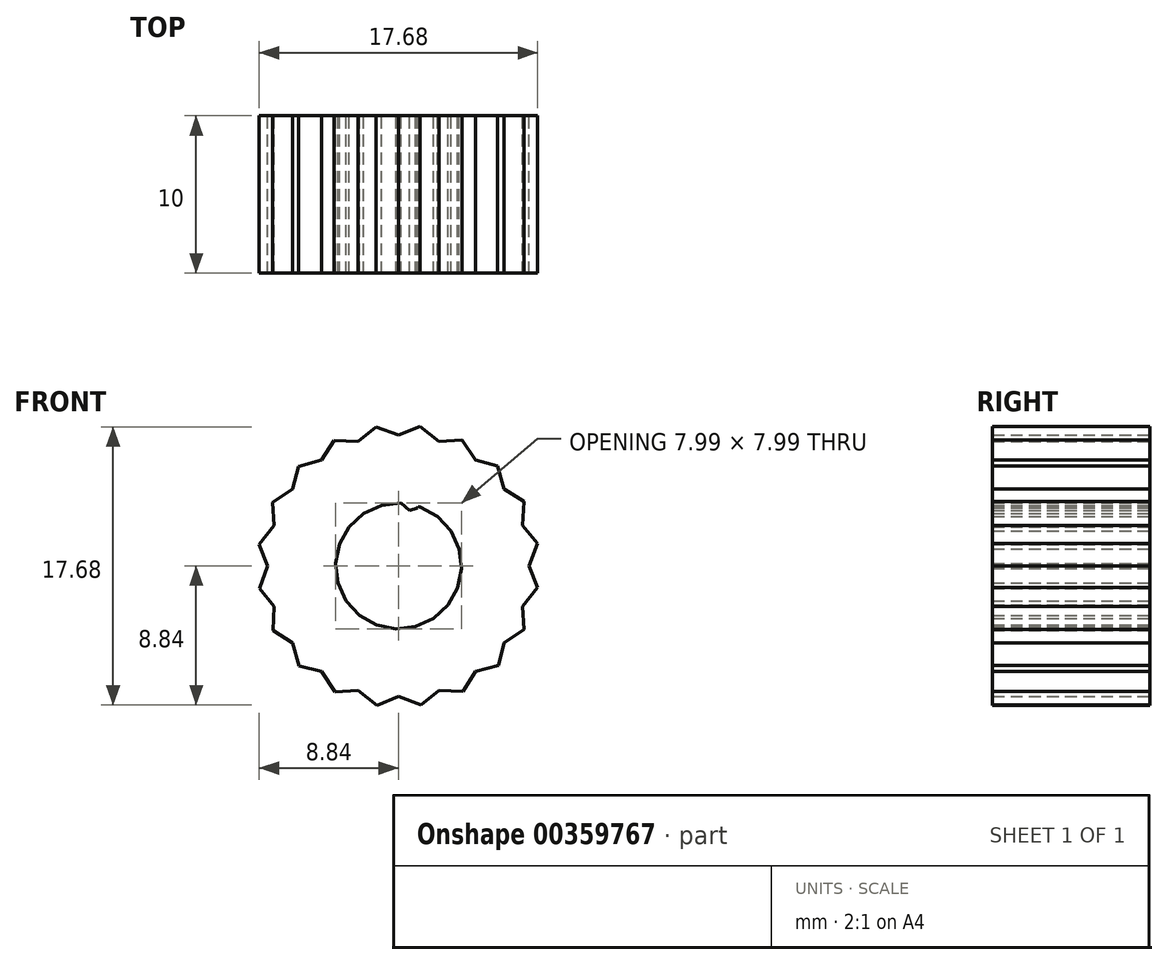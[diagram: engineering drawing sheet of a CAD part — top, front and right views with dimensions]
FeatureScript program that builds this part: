
annotation { "Feature Type Name" : "Feature", "Feature Type Description" : "" }
export const myFeature = defineFeature(function(context is Context, id is Id, definition is map)
    precondition{}
    {
        {
            var Q0;
            Q0=qCreatedBy(makeId("Front.planeOp"),FACE);
            var sketch = newSketch(context, id + "F0", { "sketchPlane" : qUnion([Q0])});
            skCircle(sketch, "E0.cCircle", {"center": v(72.37, -26.07) * mm, "radius": 22.37 * mm, "construction": true});
            skLineSegment(sketch, "E0.0", {"start": v(80.22, -4.82) * mm, "end": v(86.4, -8.29) * mm});
            skLineSegment(sketch, "E0.1", {"start": v(86.4, -8.29) * mm, "end": v(91.21, -13.5) * mm});
            skLineSegment(sketch, "E0.2", {"start": v(91.21, -13.5) * mm, "end": v(94.18, -19.93) * mm});
            skLineSegment(sketch, "E0.3", {"start": v(94.18, -19.93) * mm, "end": v(95, -26.97) * mm});
            skLineSegment(sketch, "E0.4", {"start": v(95, -26.97) * mm, "end": v(93.62, -33.92) * mm});
            skLineSegment(sketch, "E0.5", {"start": v(93.62, -33.92) * mm, "end": v(90.16, -40.1) * mm});
            skLineSegment(sketch, "E0.6", {"start": v(90.16, -40.1) * mm, "end": v(84.95, -44.91) * mm});
            skLineSegment(sketch, "E0.7", {"start": v(84.95, -44.91) * mm, "end": v(78.51, -47.87) * mm});
            skLineSegment(sketch, "E0.8", {"start": v(78.51, -47.87) * mm, "end": v(71.47, -48.7) * mm});
            skLineSegment(sketch, "E0.9", {"start": v(71.47, -48.7) * mm, "end": v(64.52, -47.32) * mm});
            skLineSegment(sketch, "E0.10", {"start": v(64.52, -47.32) * mm, "end": v(58.34, -43.85) * mm});
            skLineSegment(sketch, "E0.11", {"start": v(58.34, -43.85) * mm, "end": v(53.53, -38.64) * mm});
            skLineSegment(sketch, "E0.12", {"start": v(53.53, -38.64) * mm, "end": v(50.57, -32.2) * mm});
            skLineSegment(sketch, "E0.13", {"start": v(50.57, -32.2) * mm, "end": v(49.74, -25.17) * mm});
            skLineSegment(sketch, "E0.14", {"start": v(49.74, -25.17) * mm, "end": v(51.13, -18.22) * mm});
            skLineSegment(sketch, "E0.15", {"start": v(51.13, -18.22) * mm, "end": v(54.6, -12.04) * mm});
            skLineSegment(sketch, "E0.16", {"start": v(54.6, -12.04) * mm, "end": v(59.8, -7.23) * mm});
            skLineSegment(sketch, "E0.17", {"start": v(59.8, -7.23) * mm, "end": v(66.24, -4.27) * mm});
            skLineSegment(sketch, "E0.18", {"start": v(66.24, -4.27) * mm, "end": v(73.27, -3.44) * mm});
            skLineSegment(sketch, "E0.19", {"start": v(73.27, -3.44) * mm, "end": v(80.22, -4.82) * mm});
            skPoint(sketch, "E0.0.midPoint", {"position": v(83.32, -6.56) * mm});
            skCircle(sketch, "E1.cCircle", {"center": v(0, 0) * mm, "radius": 8.2 * mm, "construction": true});
            skLineSegment(sketch, "E1.0", {"start": v(4.88, -6.72) * mm, "end": v(2.57, -7.9) * mm});
            skLineSegment(sketch, "E1.1", {"start": v(2.57, -7.9) * mm, "end": v(0, -8.3) * mm});
            skLineSegment(sketch, "E1.2", {"start": v(0, -8.3) * mm, "end": v(-2.57, -7.9) * mm});
            skLineSegment(sketch, "E1.3", {"start": v(-2.57, -7.9) * mm, "end": v(-4.88, -6.72) * mm});
            skLineSegment(sketch, "E1.4", {"start": v(-4.88, -6.72) * mm, "end": v(-6.72, -4.88) * mm});
            skLineSegment(sketch, "E1.5", {"start": v(-6.72, -4.88) * mm, "end": v(-7.9, -2.57) * mm});
            skLineSegment(sketch, "E1.6", {"start": v(-7.9, -2.57) * mm, "end": v(-8.3, 0) * mm});
            skLineSegment(sketch, "E1.7", {"start": v(-8.3, 0) * mm, "end": v(-7.9, 2.57) * mm});
            skLineSegment(sketch, "E1.8", {"start": v(-7.9, 2.57) * mm, "end": v(-6.72, 4.88) * mm});
            skLineSegment(sketch, "E1.9", {"start": v(-6.72, 4.88) * mm, "end": v(-4.88, 6.72) * mm});
            skLineSegment(sketch, "E1.10", {"start": v(-4.88, 6.72) * mm, "end": v(-2.57, 7.9) * mm});
            skLineSegment(sketch, "E1.11", {"start": v(-2.57, 7.9) * mm, "end": v(0, 8.3) * mm});
            skLineSegment(sketch, "E1.12", {"start": v(0, 8.3) * mm, "end": v(2.57, 7.9) * mm});
            skLineSegment(sketch, "E1.13", {"start": v(2.57, 7.9) * mm, "end": v(4.88, 6.72) * mm});
            skLineSegment(sketch, "E1.14", {"start": v(4.88, 6.72) * mm, "end": v(6.72, 4.88) * mm});
            skLineSegment(sketch, "E1.15", {"start": v(6.72, 4.88) * mm, "end": v(7.9, 2.57) * mm});
            skLineSegment(sketch, "E1.16", {"start": v(7.9, 2.57) * mm, "end": v(8.3, 0) * mm});
            skLineSegment(sketch, "E1.17", {"start": v(8.3, 0) * mm, "end": v(7.9, -2.57) * mm});
            skLineSegment(sketch, "E1.18", {"start": v(7.9, -2.57) * mm, "end": v(6.72, -4.88) * mm});
            skLineSegment(sketch, "E1.19", {"start": v(6.72, -4.88) * mm, "end": v(4.88, -6.72) * mm});
            skPoint(sketch, "E1.0.midPoint", {"position": v(3.72, -7.3) * mm});
            skCircle(sketch, "E2", {"center": v(0, 0) * mm, "radius": 8.95 * mm});
            skLineSegment(sketch, "E3", {"start": v(0, 8.3) * mm, "end": v(1.37, 8.84) * mm});
            skLineSegment(sketch, "E4", {"start": v(1.37, 8.84) * mm, "end": v(2.57, 7.9) * mm});
            skLineSegment(sketch, "E5", {"start": v(0, 0) * mm, "end": v(5.29, 16.27) * mm});
            skLineSegment(sketch, "E6.1.0", {"start": v(-2.57, 7.9) * mm, "end": v(-1.43, 8.84) * mm});
            skLineSegment(sketch, "E6.1.1", {"start": v(-1.43, 8.84) * mm, "end": v(0, 8.3) * mm});
            skLineSegment(sketch, "E6.2.0", {"start": v(-4.88, 6.72) * mm, "end": v(-4.09, 7.96) * mm});
            skLineSegment(sketch, "E6.2.1", {"start": v(-4.09, 7.96) * mm, "end": v(-2.57, 7.9) * mm});
            skLineSegment(sketch, "E6.3.0", {"start": v(-6.72, 4.88) * mm, "end": v(-6.35, 6.3) * mm});
            skLineSegment(sketch, "E6.3.1", {"start": v(-6.35, 6.3) * mm, "end": v(-4.88, 6.72) * mm});
            skLineSegment(sketch, "E6.4.0", {"start": v(-7.9, 2.57) * mm, "end": v(-7.99, 4.04) * mm});
            skLineSegment(sketch, "E6.4.1", {"start": v(-7.99, 4.04) * mm, "end": v(-6.72, 4.88) * mm});
            skLineSegment(sketch, "E6.5.0", {"start": v(-8.3, 0) * mm, "end": v(-8.84, 1.37) * mm});
            skLineSegment(sketch, "E6.5.1", {"start": v(-8.84, 1.37) * mm, "end": v(-7.9, 2.57) * mm});
            skLineSegment(sketch, "E6.6.0", {"start": v(-7.9, -2.57) * mm, "end": v(-8.84, -1.43) * mm});
            skLineSegment(sketch, "E6.6.1", {"start": v(-8.84, -1.43) * mm, "end": v(-8.3, 0) * mm});
            skLineSegment(sketch, "E6.7.0", {"start": v(-6.72, -4.88) * mm, "end": v(-7.96, -4.09) * mm});
            skLineSegment(sketch, "E6.7.1", {"start": v(-7.96, -4.09) * mm, "end": v(-7.9, -2.57) * mm});
            skLineSegment(sketch, "E6.8.0", {"start": v(-4.88, -6.72) * mm, "end": v(-6.3, -6.35) * mm});
            skLineSegment(sketch, "E6.8.1", {"start": v(-6.3, -6.35) * mm, "end": v(-6.72, -4.88) * mm});
            skLineSegment(sketch, "E6.9.0", {"start": v(-2.57, -7.9) * mm, "end": v(-4.04, -7.99) * mm});
            skLineSegment(sketch, "E6.9.1", {"start": v(-4.04, -7.99) * mm, "end": v(-4.88, -6.72) * mm});
            skLineSegment(sketch, "E6.10.0", {"start": v(0, -8.3) * mm, "end": v(-1.37, -8.84) * mm});
            skLineSegment(sketch, "E6.10.1", {"start": v(-1.37, -8.84) * mm, "end": v(-2.57, -7.9) * mm});
            skLineSegment(sketch, "E6.11.0", {"start": v(2.57, -7.9) * mm, "end": v(1.43, -8.84) * mm});
            skLineSegment(sketch, "E6.11.1", {"start": v(1.43, -8.84) * mm, "end": v(0, -8.3) * mm});
            skLineSegment(sketch, "E6.12.0", {"start": v(4.88, -6.72) * mm, "end": v(4.09, -7.96) * mm});
            skLineSegment(sketch, "E6.12.1", {"start": v(4.09, -7.96) * mm, "end": v(2.57, -7.9) * mm});
            skLineSegment(sketch, "E6.13.0", {"start": v(6.72, -4.88) * mm, "end": v(6.35, -6.3) * mm});
            skLineSegment(sketch, "E6.13.1", {"start": v(6.35, -6.3) * mm, "end": v(4.88, -6.72) * mm});
            skLineSegment(sketch, "E6.14.0", {"start": v(7.9, -2.57) * mm, "end": v(7.99, -4.04) * mm});
            skLineSegment(sketch, "E6.14.1", {"start": v(7.99, -4.04) * mm, "end": v(6.72, -4.88) * mm});
            skLineSegment(sketch, "E6.15.0", {"start": v(8.3, 0) * mm, "end": v(8.84, -1.37) * mm});
            skLineSegment(sketch, "E6.15.1", {"start": v(8.84, -1.37) * mm, "end": v(7.9, -2.57) * mm});
            skLineSegment(sketch, "E6.16.0", {"start": v(7.9, 2.57) * mm, "end": v(8.84, 1.43) * mm});
            skLineSegment(sketch, "E6.16.1", {"start": v(8.84, 1.43) * mm, "end": v(8.3, 0) * mm});
            skLineSegment(sketch, "E6.17.0", {"start": v(6.72, 4.88) * mm, "end": v(7.96, 4.09) * mm});
            skLineSegment(sketch, "E6.17.1", {"start": v(7.96, 4.09) * mm, "end": v(7.9, 2.57) * mm});
            skLineSegment(sketch, "E6.18.0", {"start": v(4.88, 6.72) * mm, "end": v(6.3, 6.35) * mm});
            skLineSegment(sketch, "E6.18.1", {"start": v(6.3, 6.35) * mm, "end": v(6.72, 4.88) * mm});
            skLineSegment(sketch, "E6.19.0", {"start": v(2.57, 7.9) * mm, "end": v(4.04, 7.99) * mm});
            skLineSegment(sketch, "E6.19.1", {"start": v(4.04, 7.99) * mm, "end": v(4.88, 6.72) * mm});
            skCircle(sketch, "E7", {"center": v(0, 0) * mm, "radius": 3.6 * mm});
            skCircle(sketch, "E8.cCircle", {"center": v(0, 0) * mm, "radius": 4 * mm, "construction": true});
            skLineSegment(sketch, "E8.0", {"start": v(2.48, 3.14) * mm, "end": v(3.33, 2.22) * mm});
            skLineSegment(sketch, "E8.1", {"start": v(3.33, 2.22) * mm, "end": v(3.85, 1.08) * mm});
            skLineSegment(sketch, "E8.2", {"start": v(3.85, 1.08) * mm, "end": v(4, -0.16) * mm});
            skLineSegment(sketch, "E8.3", {"start": v(4, -0.16) * mm, "end": v(3.75, -1.39) * mm});
            skLineSegment(sketch, "E8.4", {"start": v(3.75, -1.39) * mm, "end": v(3.14, -2.48) * mm});
            skLineSegment(sketch, "E8.5", {"start": v(3.14, -2.48) * mm, "end": v(2.22, -3.33) * mm});
            skLineSegment(sketch, "E8.6", {"start": v(2.22, -3.33) * mm, "end": v(1.08, -3.85) * mm});
            skLineSegment(sketch, "E8.7", {"start": v(1.08, -3.85) * mm, "end": v(-0.16, -4) * mm});
            skLineSegment(sketch, "E8.8", {"start": v(-0.16, -4) * mm, "end": v(-1.39, -3.75) * mm});
            skLineSegment(sketch, "E8.9", {"start": v(-1.39, -3.75) * mm, "end": v(-2.48, -3.14) * mm});
            skLineSegment(sketch, "E8.10", {"start": v(-2.48, -3.14) * mm, "end": v(-3.33, -2.22) * mm});
            skLineSegment(sketch, "E8.11", {"start": v(-3.33, -2.22) * mm, "end": v(-3.85, -1.08) * mm});
            skLineSegment(sketch, "E8.12", {"start": v(-3.85, -1.08) * mm, "end": v(-4, 0.16) * mm});
            skLineSegment(sketch, "E8.13", {"start": v(-4, 0.16) * mm, "end": v(-3.75, 1.39) * mm});
            skLineSegment(sketch, "E8.14", {"start": v(-3.75, 1.39) * mm, "end": v(-3.14, 2.48) * mm});
            skLineSegment(sketch, "E8.15", {"start": v(-3.14, 2.48) * mm, "end": v(-2.22, 3.33) * mm});
            skLineSegment(sketch, "E8.16", {"start": v(-2.22, 3.33) * mm, "end": v(-1.08, 3.85) * mm});
            skLineSegment(sketch, "E8.17", {"start": v(-1.08, 3.85) * mm, "end": v(0.16, 4) * mm});
            skLineSegment(sketch, "E8.18", {"start": v(0.16, 4) * mm, "end": v(1.39, 3.75) * mm});
            skLineSegment(sketch, "E8.19", {"start": v(1.39, 3.75) * mm, "end": v(2.48, 3.14) * mm});
            skLineSegment(sketch, "E9", {"start": v(-2.48, -3.14) * mm, "end": v(-1.39, -3.75) * mm});
            skLineSegment(sketch, "E10", {"start": v(-1.76, -3.14) * mm, "end": v(-2.48, -3.14) * mm});
            skLineSegment(sketch, "E11", {"start": v(-1.39, -3.75) * mm, "end": v(-1.76, -3.14) * mm});
            skLineSegment(sketch, "E12.1.1", {"start": v(-0.7, -3.53) * mm, "end": v(-1.39, -3.75) * mm});
            skLineSegment(sketch, "E12.1.2", {"start": v(-0.16, -4) * mm, "end": v(-0.7, -3.53) * mm});
            skLineSegment(sketch, "E12.2.1", {"start": v(0.42, -3.58) * mm, "end": v(-0.16, -4) * mm});
            skLineSegment(sketch, "E12.2.2", {"start": v(1.08, -3.85) * mm, "end": v(0.42, -3.58) * mm});
            skLineSegment(sketch, "E12.3.1", {"start": v(1.5, -3.27) * mm, "end": v(1.08, -3.85) * mm});
            skLineSegment(sketch, "E12.3.2", {"start": v(2.22, -3.33) * mm, "end": v(1.5, -3.27) * mm});
            skLineSegment(sketch, "E12.4.1", {"start": v(2.44, -2.64) * mm, "end": v(2.22, -3.33) * mm});
            skLineSegment(sketch, "E12.4.2", {"start": v(3.14, -2.48) * mm, "end": v(2.44, -2.64) * mm});
            skLineSegment(sketch, "E12.5.1", {"start": v(3.14, -1.76) * mm, "end": v(3.14, -2.48) * mm});
            skLineSegment(sketch, "E12.5.2", {"start": v(3.75, -1.39) * mm, "end": v(3.14, -1.76) * mm});
            skLineSegment(sketch, "E12.6.1", {"start": v(3.53, -0.7) * mm, "end": v(3.75, -1.39) * mm});
            skLineSegment(sketch, "E12.6.2", {"start": v(4, -0.16) * mm, "end": v(3.53, -0.7) * mm});
            skLineSegment(sketch, "E12.7.1", {"start": v(3.58, 0.42) * mm, "end": v(4, -0.16) * mm});
            skLineSegment(sketch, "E12.7.2", {"start": v(3.85, 1.08) * mm, "end": v(3.58, 0.42) * mm});
            skLineSegment(sketch, "E12.8.1", {"start": v(3.27, 1.5) * mm, "end": v(3.85, 1.08) * mm});
            skLineSegment(sketch, "E12.8.2", {"start": v(3.33, 2.22) * mm, "end": v(3.27, 1.5) * mm});
            skLineSegment(sketch, "E12.9.1", {"start": v(2.64, 2.44) * mm, "end": v(3.33, 2.22) * mm});
            skLineSegment(sketch, "E12.9.2", {"start": v(2.48, 3.14) * mm, "end": v(2.64, 2.44) * mm});
            skLineSegment(sketch, "E12.10.1", {"start": v(1.76, 3.14) * mm, "end": v(2.48, 3.14) * mm});
            skLineSegment(sketch, "E12.10.2", {"start": v(1.39, 3.75) * mm, "end": v(1.76, 3.14) * mm});
            skLineSegment(sketch, "E12.11.1", {"start": v(0.7, 3.53) * mm, "end": v(1.39, 3.75) * mm});
            skLineSegment(sketch, "E12.11.2", {"start": v(0.16, 4) * mm, "end": v(0.7, 3.53) * mm});
            skLineSegment(sketch, "E12.12.1", {"start": v(-0.42, 3.58) * mm, "end": v(0.16, 4) * mm});
            skLineSegment(sketch, "E12.12.2", {"start": v(-1.08, 3.85) * mm, "end": v(-0.42, 3.58) * mm});
            skLineSegment(sketch, "E12.13.1", {"start": v(-1.5, 3.27) * mm, "end": v(-1.08, 3.85) * mm});
            skLineSegment(sketch, "E12.13.2", {"start": v(-2.22, 3.33) * mm, "end": v(-1.5, 3.27) * mm});
            skLineSegment(sketch, "E12.14.1", {"start": v(-2.44, 2.64) * mm, "end": v(-2.22, 3.33) * mm});
            skLineSegment(sketch, "E12.14.2", {"start": v(-3.14, 2.48) * mm, "end": v(-2.44, 2.64) * mm});
            skLineSegment(sketch, "E12.15.1", {"start": v(-3.14, 1.76) * mm, "end": v(-3.14, 2.48) * mm});
            skLineSegment(sketch, "E12.15.2", {"start": v(-3.75, 1.39) * mm, "end": v(-3.14, 1.76) * mm});
            skLineSegment(sketch, "E12.16.1", {"start": v(-3.53, 0.7) * mm, "end": v(-3.75, 1.39) * mm});
            skLineSegment(sketch, "E12.16.2", {"start": v(-4, 0.16) * mm, "end": v(-3.53, 0.7) * mm});
            skLineSegment(sketch, "E12.17.1", {"start": v(-3.58, -0.42) * mm, "end": v(-4, 0.16) * mm});
            skLineSegment(sketch, "E12.17.2", {"start": v(-3.85, -1.08) * mm, "end": v(-3.58, -0.42) * mm});
            skLineSegment(sketch, "E12.18.1", {"start": v(-3.27, -1.5) * mm, "end": v(-3.85, -1.08) * mm});
            skLineSegment(sketch, "E12.18.2", {"start": v(-3.33, -2.22) * mm, "end": v(-3.27, -1.5) * mm});
            skLineSegment(sketch, "E12.19.1", {"start": v(-2.64, -2.44) * mm, "end": v(-3.33, -2.22) * mm});
            skLineSegment(sketch, "E12.19.2", {"start": v(-2.48, -3.14) * mm, "end": v(-2.64, -2.44) * mm});
            skSolve(sketch);
        }
        {
            var Q0;
            Q0=makeQuery(id+"F0.imprint","IMPRINT",FACE,{"disambiguationData":[TD([[makeQuery(id+"F0.imprint","IMPRINT",EDGE,{"derivedFrom":sQuery(id+"F0.wireOp",EDGE,"E6.3.0")}),-1.0]])]});
            var Q1;
            Q1=makeQuery(id+"F0.imprint","IMPRINT",FACE,{"disambiguationData":[TD([[makeQuery(id+"F0.imprint","IMPRINT",EDGE,{"derivedFrom":sQuery(id+"F0.wireOp",EDGE,"E6.2.0")}),-1.0]])]});
            var Q2;
            Q2=makeQuery(id+"F0.imprint","IMPRINT",FACE,{"disambiguationData":[TD([[makeQuery(id+"F0.imprint","IMPRINT",EDGE,{"derivedFrom":sQuery(id+"F0.wireOp",EDGE,"E6.1.0")}),-1.0]])]});
            var Q3;
            Q3=makeQuery(id+"F0.imprint","IMPRINT",FACE,{"disambiguationData":[TD([[makeQuery(id+"F0.imprint","IMPRINT",EDGE,{"derivedFrom":sQuery(id+"F0.wireOp",EDGE,"E1.12")}),1.0]])]});
            var Q4;
            Q4=makeQuery(id+"F0.imprint","IMPRINT",FACE,{"disambiguationData":[TD([[makeQuery(id+"F0.imprint","IMPRINT",EDGE,{"derivedFrom":sQuery(id+"F0.wireOp",EDGE,"E6.19.0")}),-1.0]])]});
            var Q5;
            Q5=makeQuery(id+"F0.imprint","IMPRINT",FACE,{"disambiguationData":[TD([[makeQuery(id+"F0.imprint","IMPRINT",EDGE,{"derivedFrom":sQuery(id+"F0.wireOp",EDGE,"E6.18.0")}),-1.0]])]});
            var Q6;
            Q6=makeQuery(id+"F0.imprint","IMPRINT",FACE,{"disambiguationData":[TD([[makeQuery(id+"F0.imprint","IMPRINT",EDGE,{"derivedFrom":sQuery(id+"F0.wireOp",EDGE,"E6.17.0")}),-1.0]])]});
            var Q7;
            Q7=makeQuery(id+"F0.imprint","IMPRINT",FACE,{"disambiguationData":[TD([[makeQuery(id+"F0.imprint","IMPRINT",EDGE,{"derivedFrom":sQuery(id+"F0.wireOp",EDGE,"E6.16.0")}),-1.0]])]});
            var Q8;
            Q8=makeQuery(id+"F0.imprint","IMPRINT",FACE,{"disambiguationData":[TD([[makeQuery(id+"F0.imprint","IMPRINT",EDGE,{"derivedFrom":sQuery(id+"F0.wireOp",EDGE,"E6.15.0")}),-1.0]])]});
            var Q9;
            Q9=makeQuery(id+"F0.imprint","IMPRINT",FACE,{"disambiguationData":[TD([[makeQuery(id+"F0.imprint","IMPRINT",EDGE,{"derivedFrom":sQuery(id+"F0.wireOp",EDGE,"E6.14.0")}),-1.0]])]});
            var Q10;
            Q10=makeQuery(id+"F0.imprint","IMPRINT",FACE,{"disambiguationData":[TD([[makeQuery(id+"F0.imprint","IMPRINT",EDGE,{"derivedFrom":sQuery(id+"F0.wireOp",EDGE,"E6.13.0")}),-1.0]])]});
            var Q11;
            Q11=makeQuery(id+"F0.imprint","IMPRINT",FACE,{"disambiguationData":[TD([[makeQuery(id+"F0.imprint","IMPRINT",EDGE,{"derivedFrom":sQuery(id+"F0.wireOp",EDGE,"E6.12.0")}),-1.0]])]});
            var Q12;
            Q12=makeQuery(id+"F0.imprint","IMPRINT",FACE,{"disambiguationData":[TD([[makeQuery(id+"F0.imprint","IMPRINT",EDGE,{"derivedFrom":sQuery(id+"F0.wireOp",EDGE,"E6.11.0")}),-1.0]])]});
            var Q13;
            Q13=makeQuery(id+"F0.imprint","IMPRINT",FACE,{"disambiguationData":[TD([[makeQuery(id+"F0.imprint","IMPRINT",EDGE,{"derivedFrom":sQuery(id+"F0.wireOp",EDGE,"E6.10.0")}),-1.0]])]});
            var Q14;
            Q14=makeQuery(id+"F0.imprint","IMPRINT",FACE,{"disambiguationData":[TD([[makeQuery(id+"F0.imprint","IMPRINT",EDGE,{"derivedFrom":sQuery(id+"F0.wireOp",EDGE,"E6.9.0")}),-1.0]])]});
            var Q15;
            Q15=makeQuery(id+"F0.imprint","IMPRINT",FACE,{"disambiguationData":[TD([[makeQuery(id+"F0.imprint","IMPRINT",EDGE,{"derivedFrom":sQuery(id+"F0.wireOp",EDGE,"E6.8.0")}),-1.0]])]});
            var Q16;
            Q16=makeQuery(id+"F0.imprint","IMPRINT",FACE,{"disambiguationData":[TD([[makeQuery(id+"F0.imprint","IMPRINT",EDGE,{"derivedFrom":sQuery(id+"F0.wireOp",EDGE,"E6.7.0")}),-1.0]])]});
            var Q17;
            Q17=makeQuery(id+"F0.imprint","IMPRINT",FACE,{"disambiguationData":[TD([[makeQuery(id+"F0.imprint","IMPRINT",EDGE,{"derivedFrom":sQuery(id+"F0.wireOp",EDGE,"E6.6.0")}),-1.0]])]});
            var Q18;
            Q18=makeQuery(id+"F0.imprint","IMPRINT",FACE,{"disambiguationData":[TD([[makeQuery(id+"F0.imprint","IMPRINT",EDGE,{"derivedFrom":sQuery(id+"F0.wireOp",EDGE,"E6.4.0")}),-1.0]])]});
            var Q19;
            Q19=makeQuery(id+"F0.imprint","IMPRINT",FACE,{"disambiguationData":[TD([[makeQuery(id+"F0.imprint","IMPRINT",EDGE,{"derivedFrom":sQuery(id+"F0.wireOp",EDGE,"E6.5.0")}),-1.0]])]});
            var Q20;
            Q20=makeQuery(id+"F0.imprint","IMPRINT",FACE,{"disambiguationData":[TD([[makeQuery(id+"F0.imprint","IMPRINT",EDGE,{"derivedFrom":sQuery(id+"F0.wireOp",EDGE,"E9")}),1.0]])]});
            var Q21;
            Q21=makeQuery(id+"F0.imprint","IMPRINT",FACE,{"disambiguationData":[TD([[makeQuery(id+"F0.imprint","IMPRINT",EDGE,{"derivedFrom":sQuery(id+"F0.wireOp",EDGE,"E8.8")}),-1.0]])]});
            var Q22;
            Q22=makeQuery(id+"F0.imprint","IMPRINT",FACE,{"disambiguationData":[TD([[makeQuery(id+"F0.imprint","IMPRINT",EDGE,{"derivedFrom":sQuery(id+"F0.wireOp",EDGE,"E8.7")}),-1.0]])]});
            var Q23;
            Q23=makeQuery(id+"F0.imprint","IMPRINT",FACE,{"disambiguationData":[TD([[makeQuery(id+"F0.imprint","IMPRINT",EDGE,{"derivedFrom":sQuery(id+"F0.wireOp",EDGE,"E8.6")}),-1.0]])]});
            var Q24;
            Q24=makeQuery(id+"F0.imprint","IMPRINT",FACE,{"disambiguationData":[TD([[makeQuery(id+"F0.imprint","IMPRINT",EDGE,{"derivedFrom":sQuery(id+"F0.wireOp",EDGE,"E8.5")}),-1.0]])]});
            var Q25;
            Q25=makeQuery(id+"F0.imprint","IMPRINT",FACE,{"disambiguationData":[TD([[makeQuery(id+"F0.imprint","IMPRINT",EDGE,{"derivedFrom":sQuery(id+"F0.wireOp",EDGE,"E8.4")}),-1.0]])]});
            var Q26;
            Q26=makeQuery(id+"F0.imprint","IMPRINT",FACE,{"disambiguationData":[TD([[makeQuery(id+"F0.imprint","IMPRINT",EDGE,{"derivedFrom":sQuery(id+"F0.wireOp",EDGE,"E8.3")}),-1.0]])]});
            var Q27;
            Q27=makeQuery(id+"F0.imprint","IMPRINT",FACE,{"disambiguationData":[TD([[makeQuery(id+"F0.imprint","IMPRINT",EDGE,{"derivedFrom":sQuery(id+"F0.wireOp",EDGE,"E8.2")}),-1.0]])]});
            var Q28;
            Q28=makeQuery(id+"F0.imprint","IMPRINT",FACE,{"disambiguationData":[TD([[makeQuery(id+"F0.imprint","IMPRINT",EDGE,{"derivedFrom":sQuery(id+"F0.wireOp",EDGE,"E8.1")}),-1.0]])]});
            var Q29;
            Q29=makeQuery(id+"F0.imprint","IMPRINT",FACE,{"disambiguationData":[TD([[makeQuery(id+"F0.imprint","IMPRINT",EDGE,{"derivedFrom":sQuery(id+"F0.wireOp",EDGE,"E8.0")}),-1.0]])]});
            var Q30;
            Q30=makeQuery(id+"F0.imprint","IMPRINT",FACE,{"disambiguationData":[TD([[makeQuery(id+"F0.imprint","IMPRINT",EDGE,{"derivedFrom":sQuery(id+"F0.wireOp",EDGE,"E8.19")}),-1.0]])]});
            var Q31;
            {var subQ5=sQuery(id+"F0.wireOp",EDGE,"E12.11.2");Q31=makeQuery(id+"F0.imprint","IMPRINT",FACE,{"disambiguationData":[TD([[makeQuery(id+"F0.imprint","IMPRINT",EDGE,{"derivedFrom":subQ5}),1.0]])]});}
            var Q32;
            Q32=makeQuery(id+"F0.imprint","IMPRINT",FACE,{"disambiguationData":[TD([[makeQuery(id+"F0.imprint","IMPRINT",EDGE,{"derivedFrom":sQuery(id+"F0.wireOp",EDGE,"E8.11")}),-1.0]])]});
            var Q33;
            Q33=makeQuery(id+"F0.imprint","IMPRINT",FACE,{"disambiguationData":[TD([[makeQuery(id+"F0.imprint","IMPRINT",EDGE,{"derivedFrom":sQuery(id+"F0.wireOp",EDGE,"E1.12")}),-1.0]])]});
            var Q34;
            Q34=makeQuery(id+"F0.imprint","IMPRINT",FACE,{"disambiguationData":[TD([[makeQuery(id+"F0.imprint","IMPRINT",EDGE,{"derivedFrom":sQuery(id+"F0.wireOp",EDGE,"E8.15")}),-1.0]])]});
            var Q35;
            Q35=makeQuery(id+"F0.imprint","IMPRINT",FACE,{"disambiguationData":[TD([[makeQuery(id+"F0.imprint","IMPRINT",EDGE,{"derivedFrom":sQuery(id+"F0.wireOp",EDGE,"E8.16")}),-1.0]])]});
            var Q36;
            Q36=makeQuery(id+"F0.imprint","IMPRINT",FACE,{"disambiguationData":[TD([[makeQuery(id+"F0.imprint","IMPRINT",EDGE,{"derivedFrom":sQuery(id+"F0.wireOp",EDGE,"E8.17")}),-1.0]])]});
            var Q37;
            Q37=makeQuery(id+"F0.imprint","IMPRINT",FACE,{"disambiguationData":[TD([[makeQuery(id+"F0.imprint","IMPRINT",EDGE,{"derivedFrom":sQuery(id+"F0.wireOp",EDGE,"E8.14")}),-1.0]])]});
            var Q38;
            Q38=makeQuery(id+"F0.imprint","IMPRINT",FACE,{"disambiguationData":[TD([[makeQuery(id+"F0.imprint","IMPRINT",EDGE,{"derivedFrom":sQuery(id+"F0.wireOp",EDGE,"E8.13")}),-1.0]])]});
            var Q39;
            Q39=makeQuery(id+"F0.imprint","IMPRINT",FACE,{"disambiguationData":[TD([[makeQuery(id+"F0.imprint","IMPRINT",EDGE,{"derivedFrom":sQuery(id+"F0.wireOp",EDGE,"E8.12")}),-1.0]])]});
            var Q40;
            Q40=makeQuery(id+"F0.imprint","IMPRINT",FACE,{"disambiguationData":[TD([[makeQuery(id+"F0.imprint","IMPRINT",EDGE,{"derivedFrom":sQuery(id+"F0.wireOp",EDGE,"E8.10")}),-1.0]])]});
            extrude(context, id + "F1", {"entities" : qUnion([Q0, Q1, Q2, Q3, Q4, Q5, Q6, Q7, Q8, Q9, Q10, Q11, Q12, Q13, Q14, Q15, Q16, Q17, Q18, Q19, Q20, Q21, Q22, Q23, Q24, Q25, Q26, Q27, Q28, Q29, Q30, Q31, Q32, Q33, Q34, Q35, Q36, Q37, Q38, Q39, Q40]), "depth" : 10 * mm});
        }
    });
